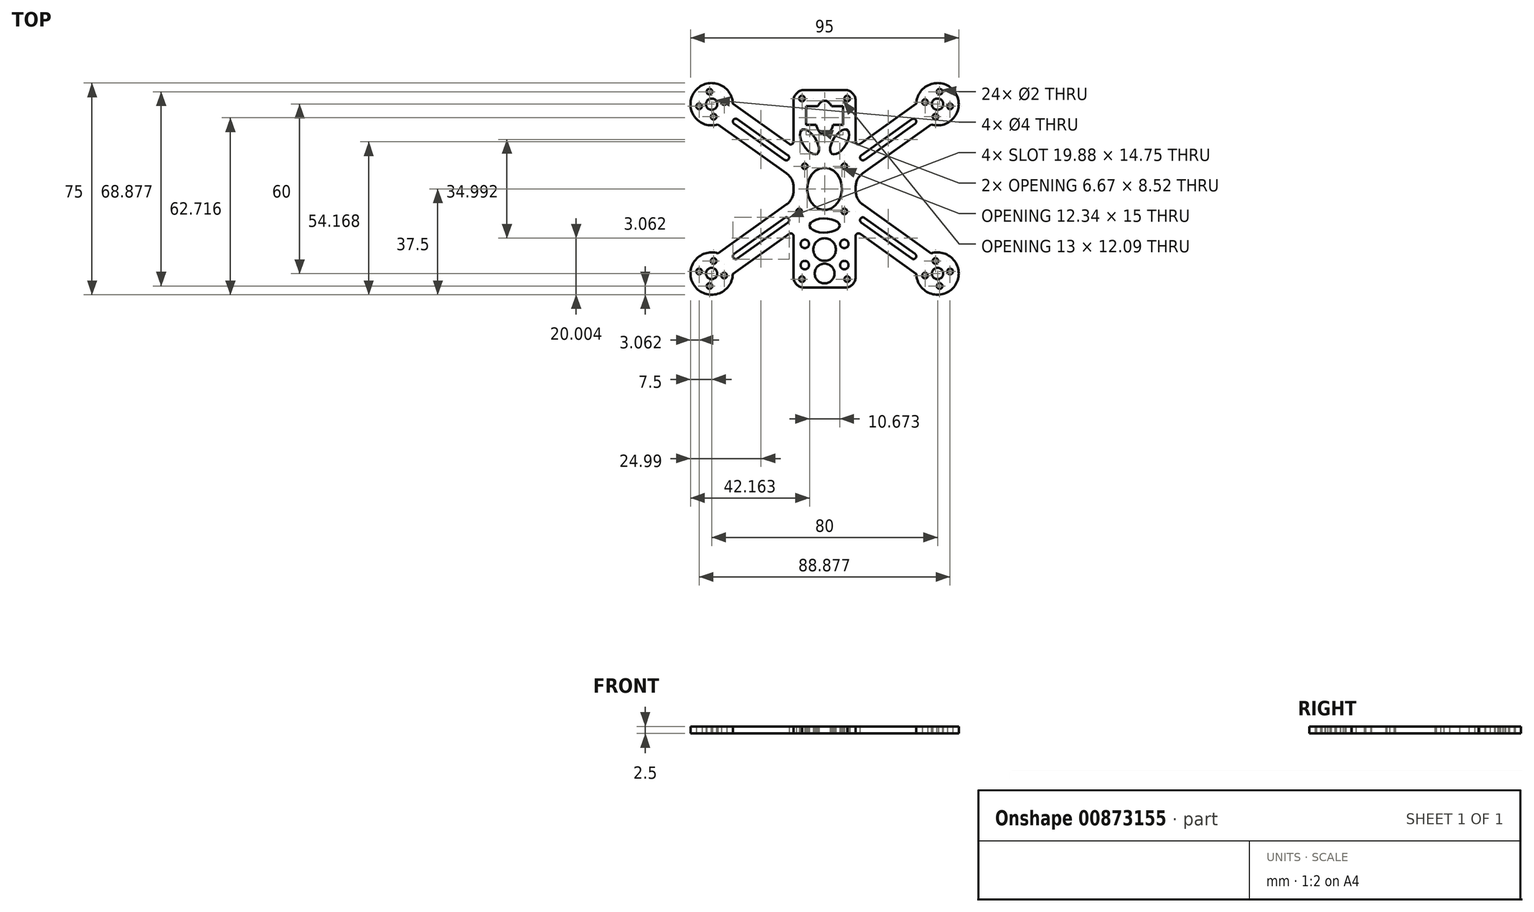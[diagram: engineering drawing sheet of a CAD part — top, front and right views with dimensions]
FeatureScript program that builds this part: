
annotation { "Feature Type Name" : "Feature", "Feature Type Description" : "" }
export const myFeature = defineFeature(function(context is Context, id is Id, definition is map)
    precondition{}
    {
        {
            var Q0;
            Q0=qCreatedBy(makeId("Top.planeOp"),FACE);
            var sketch = newSketch(context, id + "F0", { "sketchPlane" : qUnion([Q0])});
            skPoint(sketch, "E0.middle", {"position": v(0, 0) * mm});
            skCircle(sketch, "E1", {"center": v(40, 30) * mm, "radius": 7.5 * mm});
            skCircle(sketch, "E2.MirrorC", {"center": v(40, -30) * mm, "radius": 7.5 * mm});
            skCircle(sketch, "E3.MirrorC", {"center": v(-40, -30) * mm, "radius": 7.5 * mm});
            skCircle(sketch, "E4.MirrorC", {"center": v(-40, 30) * mm, "radius": 7.5 * mm});
            skCircle(sketch, "E5", {"center": v(-40, 30) * mm, "radius": 2 * mm});
            skCircle(sketch, "E6.MirrorC", {"center": v(40, 30) * mm, "radius": 2 * mm});
            skCircle(sketch, "E7.MirrorC", {"center": v(40, -30) * mm, "radius": 2 * mm});
            skCircle(sketch, "E8.MirrorC", {"center": v(-40, -30) * mm, "radius": 2 * mm});
            skLineSegment(sketch, "E9", {"start": v(12.58, 15.94) * mm, "end": v(32.5, 30.16) * mm});
            skLineSegment(sketch, "E10", {"start": v(13.51, 5.55) * mm, "end": v(37.75, 22.85) * mm});
            skLineSegment(sketch, "E11.MirrorCS", {"start": v(-13.51, 5.55) * mm, "end": v(-37.75, 22.85) * mm});
            skLineSegment(sketch, "E12.MirrorCS", {"start": v(-12.58, 15.94) * mm, "end": v(-32.5, 30.16) * mm});
            skLineSegment(sketch, "E13.MirrorCS", {"start": v(-13.51, -5.55) * mm, "end": v(-37.75, -22.85) * mm});
            skLineSegment(sketch, "E14.MirrorCS", {"start": v(13.51, -5.55) * mm, "end": v(37.75, -22.85) * mm});
            skLineSegment(sketch, "E15.MirrorCS", {"start": v(12.58, -15.94) * mm, "end": v(32.5, -30.16) * mm});
            skCircle(sketch, "E16", {"center": v(-8, 32) * mm, "radius": 1 * mm});
            skCircle(sketch, "E17.MirrorC", {"center": v(8, 32) * mm, "radius": 1 * mm});
            skCircle(sketch, "E18.MirrorC", {"center": v(-8, -32) * mm, "radius": 1 * mm});
            skCircle(sketch, "E19.MirrorC", {"center": v(8, -32) * mm, "radius": 1 * mm});
            skCircle(sketch, "E20", {"center": v(-7, 8) * mm, "radius": 1 * mm});
            skCircle(sketch, "E21.MirrorC", {"center": v(7, 8) * mm, "radius": 1 * mm});
            skCircle(sketch, "E22", {"center": v(-9, -8) * mm, "radius": 1 * mm});
            skCircle(sketch, "E23", {"center": v(7, -8) * mm, "radius": 1 * mm});
            skArc(sketch, "E24", {"start": v(-8, 35) * mm, "mid": v(-10.2, 33.53) * mm, "end": v(-11, 31) * mm});
            skArc(sketch, "E25.MirrorCS", {"start": v(8, 35) * mm, "mid": v(10.2, 33.53) * mm, "end": v(11, 31) * mm});
            skCircle(sketch, "E26.MirrorC", {"center": v(-7, -27) * mm, "radius": 1.5 * mm});
            skArc(sketch, "E27.MirrorCS", {"start": v(8, -35) * mm, "mid": v(10.2, -33.53) * mm, "end": v(11, -31) * mm});
            skArc(sketch, "E28.MirrorCS", {"start": v(-8, -35) * mm, "mid": v(-10.2, -33.53) * mm, "end": v(-11, -31) * mm});
            skLineSegment(sketch, "E29", {"start": v(-8, 35) * mm, "end": v(8, 35) * mm});
            skLineSegment(sketch, "E30", {"start": v(-11, 0.66) * mm, "end": v(-11, -0.66) * mm});
            skLineSegment(sketch, "E31", {"start": v(11, -0.66) * mm, "end": v(11, 0.66) * mm});
            skLineSegment(sketch, "E32", {"start": v(-8, -35) * mm, "end": v(8, -35) * mm});
            skCircle(sketch, "E33.MirrorC", {"center": v(-7, -19.5) * mm, "radius": 1.5 * mm});
            skPoint(sketch, "E34", {"position": v(0, -4.13) * mm});
            skPoint(sketch, "E35", {"position": v(0, -31) * mm});
            skPoint(sketch, "E36.middle", {"position": v(0, -9.01) * mm});
            skPoint(sketch, "E37", {"position": v(0, -11.87) * mm});
            skPoint(sketch, "E38", {"position": v(0, -28.6) * mm});
            skEllipse(sketch, "E39", {"center": v(0, 0) * mm, "majorRadius": 6.17 * mm, "minorRadius": 7.5 * mm, "majorAxis": v(1, 0)});
            skCircle(sketch, "E40", {"center": v(0, -21.5) * mm, "radius": 4 * mm});
            skCircle(sketch, "E41.MirrorC", {"center": v(0, -30) * mm, "radius": 3.5 * mm});
            skEllipse(sketch, "E42", {"center": v(-5.34, 16.67) * mm, "majorRadius": 5.04 * mm, "minorRadius": 2.4 * mm, "majorAxis": v(0.53, -0.85)});
            skEllipse(sketch, "E43.MirrorC", {"center": v(5.34, 16.67) * mm, "majorRadius": 5.04 * mm, "minorRadius": 2.4 * mm, "majorAxis": v(-0.53, -0.85)});
            skEllipse(sketch, "E44", {"center": v(0, -13) * mm, "majorRadius": 5.35 * mm, "minorRadius": 2.5 * mm, "majorAxis": v(1, 0)});
            skEllipse(sketch, "E45", {"center": v(0, 25.22) * mm, "majorRadius": 6.04 * mm, "minorRadius": 3.29 * mm, "majorAxis": v(0, -1)});
            skPoint(sketch, "E46.newPointA", {"position": v(-13.23, 5.34) * mm});
            skArc(sketch, "E46.filletArc", {"start": v(-11, 0.66) * mm, "mid": v(-11.67, 3.4) * mm, "end": v(-13.51, 5.55) * mm});
            skPoint(sketch, "E47.newPointA", {"position": v(13.23, 5.34) * mm});
            skArc(sketch, "E47.filletArc", {"start": v(13.51, 5.55) * mm, "mid": v(11.67, 3.4) * mm, "end": v(11, 0.66) * mm});
            skPoint(sketch, "E48.newPointA", {"position": v(13.23, -5.34) * mm});
            skArc(sketch, "E48.filletArc", {"start": v(11, -0.66) * mm, "mid": v(11.67, -3.4) * mm, "end": v(13.51, -5.55) * mm});
            skPoint(sketch, "E49.newPointA", {"position": v(-13.23, -5.34) * mm});
            skArc(sketch, "E49.filletArc", {"start": v(-13.51, -5.55) * mm, "mid": v(-11.67, -3.4) * mm, "end": v(-11, -0.66) * mm});
            skLineSegment(sketch, "E50", {"start": v(-11, 16.75) * mm, "end": v(-11, 15.39) * mm});
            skLineSegment(sketch, "E51", {"start": v(11, 16.75) * mm, "end": v(11, 15.39) * mm});
            skLineSegment(sketch, "E52", {"start": v(-11, 31) * mm, "end": v(-11, 15.39) * mm});
            skLineSegment(sketch, "E53", {"start": v(11, 31) * mm, "end": v(11, 15.39) * mm});
            skLineSegment(sketch, "E54", {"start": v(-11, -16.92) * mm, "end": v(-11, -31) * mm});
            skLineSegment(sketch, "E55", {"start": v(11, -16.75) * mm, "end": v(11, -16.92) * mm});
            skLineSegment(sketch, "E56", {"start": v(11, -16.92) * mm, "end": v(11, -31) * mm});
            skPoint(sketch, "E57.visualSharp", {"position": v(11, -14.8) * mm});
            skArc(sketch, "E57.filletArc", {"start": v(12.58, -15.94) * mm, "mid": v(11.54, -15.86) * mm, "end": v(11, -16.75) * mm});
            skArc(sketch, "E58.MirrorCS", {"start": v(-12.58, -15.94) * mm, "mid": v(-11.54, -15.86) * mm, "end": v(-11, -16.75) * mm});
            skLineSegment(sketch, "E59.MirrorCS", {"start": v(-12.58, -15.94) * mm, "end": v(-32.5, -30.16) * mm});
            skLineSegment(sketch, "E60.MirrorCS", {"start": v(-11, -16.75) * mm, "end": v(-11, -16.92) * mm});
            skPoint(sketch, "E61.visualSharp", {"position": v(-11, 14.8) * mm});
            skArc(sketch, "E61.filletArc", {"start": v(-12.58, 15.94) * mm, "mid": v(-11.54, 15.86) * mm, "end": v(-11, 16.75) * mm});
            skPoint(sketch, "E62.visualSharp", {"position": v(11, 14.8) * mm});
            skArc(sketch, "E62.filletArc", {"start": v(11, 16.75) * mm, "mid": v(11.54, 15.86) * mm, "end": v(12.58, 15.94) * mm});
            skPoint(sketch, "E63.endSnap0", {"position": v(-22.54, 23.05) * mm});
            skLineSegment(sketch, "E64", {"start": v(-40, 30) * mm, "end": v(-44.36, 23.9) * mm});
            skLineSegment(sketch, "E65", {"start": v(-40, 30) * mm, "end": v(-39.26, 25.56) * mm});
            skCircle(sketch, "E66", {"center": v(-39.26, 25.56) * mm, "radius": 1 * mm});
            skCircle(sketch, "E67.MirrorC", {"center": v(-35.56, 30.74) * mm, "radius": 1 * mm});
            skCircle(sketch, "E68.MirrorC", {"center": v(-44.44, 29.26) * mm, "radius": 1 * mm});
            skCircle(sketch, "E69.MirrorC", {"center": v(-40.74, 34.44) * mm, "radius": 1 * mm});
            skCircle(sketch, "E70.MirrorC", {"center": v(35.56, 30.74) * mm, "radius": 1 * mm});
            skCircle(sketch, "E71.MirrorC", {"center": v(40.74, 34.44) * mm, "radius": 1 * mm});
            skCircle(sketch, "E72.MirrorC", {"center": v(44.44, 29.26) * mm, "radius": 1 * mm});
            skCircle(sketch, "E73.MirrorC", {"center": v(39.26, 25.56) * mm, "radius": 1 * mm});
            skCircle(sketch, "E74.MirrorC", {"center": v(-35.56, -30.74) * mm, "radius": 1 * mm});
            skCircle(sketch, "E75.MirrorC", {"center": v(-39.26, -25.56) * mm, "radius": 1 * mm});
            skCircle(sketch, "E76.MirrorC", {"center": v(-40.74, -34.44) * mm, "radius": 1 * mm});
            skCircle(sketch, "E77.MirrorC", {"center": v(-44.44, -29.26) * mm, "radius": 1 * mm});
            skCircle(sketch, "E78.MirrorC", {"center": v(39.26, -25.56) * mm, "radius": 1 * mm});
            skCircle(sketch, "E79.MirrorC", {"center": v(44.44, -29.26) * mm, "radius": 1 * mm});
            skCircle(sketch, "E80.MirrorC", {"center": v(40.74, -34.44) * mm, "radius": 1 * mm});
            skCircle(sketch, "E81.MirrorC", {"center": v(35.56, -30.74) * mm, "radius": 1 * mm});
            skLineSegment(sketch, "E82", {"start": v(-30.88, 24.7) * mm, "end": v(-12.98, 11.92) * mm});
            skLineSegment(sketch, "E83", {"start": v(-30.88, 24.7) * mm, "end": v(-32.04, 23.07) * mm});
            skLineSegment(sketch, "E84", {"start": v(-32.04, 23.07) * mm, "end": v(-14.14, 10.3) * mm});
            skArc(sketch, "E85", {"start": v(-32.04, 23.07) * mm, "mid": v(-32.28, 24.47) * mm, "end": v(-30.88, 24.7) * mm});
            skLineSegment(sketch, "E86", {"start": v(-12.98, 11.92) * mm, "end": v(-14.14, 10.3) * mm});
            skLineSegment(sketch, "E87.MirrorCS", {"start": v(32.04, 23.07) * mm, "end": v(14.14, 10.3) * mm});
            skLineSegment(sketch, "E88.MirrorCS", {"start": v(30.88, 24.7) * mm, "end": v(12.98, 11.92) * mm});
            skArc(sketch, "E89.MirrorCS", {"start": v(32.04, 23.07) * mm, "mid": v(32.28, 24.47) * mm, "end": v(30.88, 24.7) * mm});
            skLineSegment(sketch, "E90.MirrorCS", {"start": v(-30.88, -24.7) * mm, "end": v(-12.98, -11.92) * mm});
            skLineSegment(sketch, "E91.MirrorCS", {"start": v(-32.04, -23.07) * mm, "end": v(-14.14, -10.3) * mm});
            skArc(sketch, "E92.MirrorCS", {"start": v(-32.04, -23.07) * mm, "mid": v(-32.28, -24.47) * mm, "end": v(-30.88, -24.7) * mm});
            skArc(sketch, "E93.MirrorCS", {"start": v(32.04, -23.07) * mm, "mid": v(32.28, -24.47) * mm, "end": v(30.88, -24.7) * mm});
            skLineSegment(sketch, "E94.MirrorCS", {"start": v(32.04, -23.07) * mm, "end": v(14.14, -10.3) * mm});
            skLineSegment(sketch, "E95.MirrorCS", {"start": v(30.88, -24.7) * mm, "end": v(12.98, -11.92) * mm});
            skArc(sketch, "E96", {"start": v(-12.98, 11.92) * mm, "mid": v(-12.74, 10.52) * mm, "end": v(-14.14, 10.3) * mm});
            skArc(sketch, "E97.MirrorCS", {"start": v(12.98, 11.92) * mm, "mid": v(12.74, 10.52) * mm, "end": v(14.14, 10.3) * mm});
            skArc(sketch, "E98.MirrorCS", {"start": v(12.98, -11.92) * mm, "mid": v(12.74, -10.52) * mm, "end": v(14.14, -10.3) * mm});
            skArc(sketch, "E99.MirrorCS", {"start": v(-12.98, -11.92) * mm, "mid": v(-12.74, -10.52) * mm, "end": v(-14.14, -10.3) * mm});
            skCircle(sketch, "E100.MirrorC", {"center": v(7, -19.5) * mm, "radius": 1.5 * mm});
            skCircle(sketch, "E101.MirrorC", {"center": v(7, -27) * mm, "radius": 1.5 * mm});
            skLineSegment(sketch, "E102.bottom", {"start": v(-6.5, 29.25) * mm, "end": v(6.5, 29.25) * mm});
            skLineSegment(sketch, "E102.top", {"start": v(-6.5, 22.75) * mm, "end": v(6.5, 22.75) * mm});
            skLineSegment(sketch, "E102.left", {"start": v(-6.5, 29.25) * mm, "end": v(-6.5, 22.75) * mm});
            skLineSegment(sketch, "E102.right", {"start": v(6.5, 29.25) * mm, "end": v(6.5, 22.75) * mm});
            skSolve(sketch);
        }
        {
            var Q0;
            Q0 = qSketchRegion(id + "F0", true);
            extrude(context, id + "F1", {"entities" : qUnion([Q0]), "depth" : 2.5 * mm, "offsetDistance" : 25 * mm});
        }
    });
